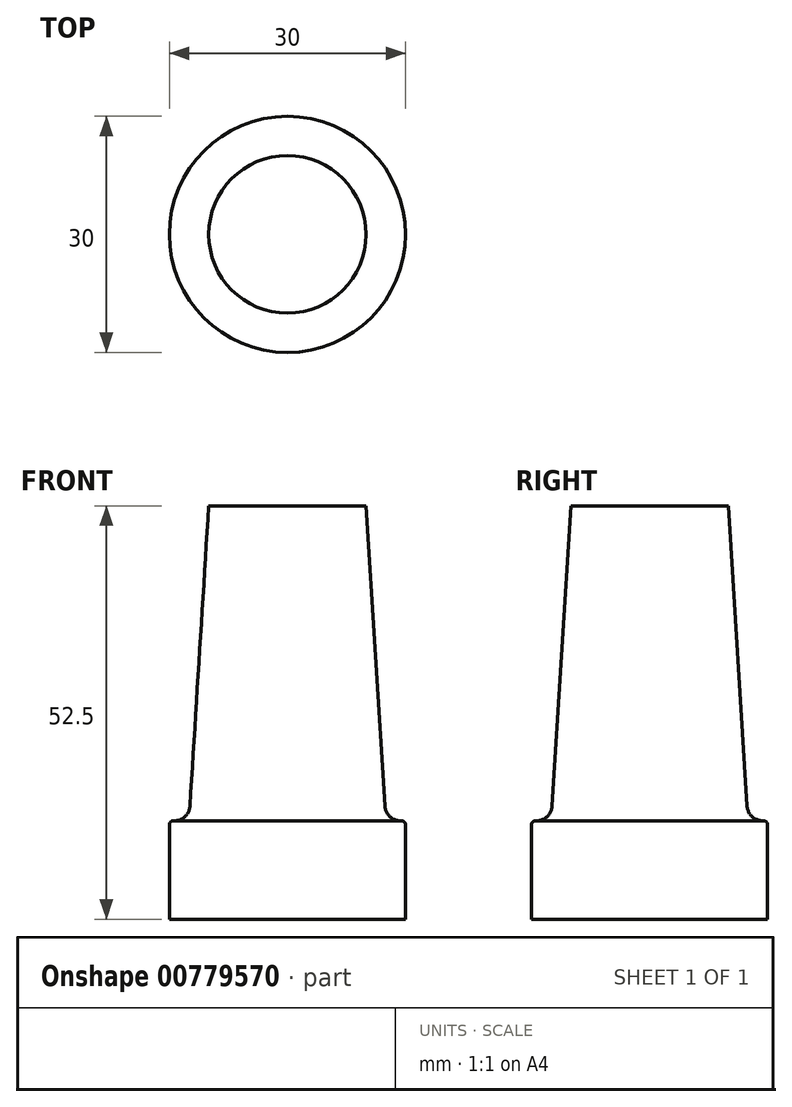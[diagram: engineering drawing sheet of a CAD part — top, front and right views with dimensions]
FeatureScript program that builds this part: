
annotation { "Feature Type Name" : "Feature", "Feature Type Description" : "" }
export const myFeature = defineFeature(function(context is Context, id is Id, definition is map)
    precondition{}
    {
        {
            var Q0;
            Q0=qCreatedBy(makeId("Front.planeOp"),FACE);
            var sketch = newSketch(context, id + "F0", { "sketchPlane" : qUnion([Q0])});
            skLineSegment(sketch, "E0.bottom", {"start": v(0, -7.5) * mm, "end": v(-15, -7.5) * mm});
            skLineSegment(sketch, "E0.left", {"start": v(15, -7.5) * mm, "end": v(15, 7.5) * mm});
            skLineSegment(sketch, "E0.right", {"start": v(-15, -7.5) * mm, "end": v(-15, 4.5) * mm});
            skPoint(sketch, "E0.middle", {"position": v(0, 0) * mm});
            skLineSegment(sketch, "E1", {"start": v(-12.38, 6.88) * mm, "end": v(-10, 45) * mm});
            skLineSegment(sketch, "E2", {"start": v(12.5, 5) * mm, "end": v(10, 45) * mm});
            skLineSegment(sketch, "E3", {"start": v(-10, 45) * mm, "end": v(0, 45) * mm});
            skLineSegment(sketch, "E4", {"start": v(12.5, 5) * mm, "end": v(-12.5, 5) * mm});
            skLineSegment(sketch, "E5", {"start": v(0, 5) * mm, "end": v(0, -7.5) * mm, "construction": true});
            skLineSegment(sketch, "E6", {"start": v(0, 5) * mm, "end": v(0, 45) * mm, "construction": true});
            skArc(sketch, "E7", {"start": v(0, 60) * mm, "mid": v(-7.5, 52.5) * mm, "end": v(0, 45) * mm});
            skLineSegment(sketch, "E8", {"start": v(-14.38, 5) * mm, "end": v(-14.5, 5) * mm});
            skPoint(sketch, "E9.visualSharp", {"position": v(-12.5, 5) * mm});
            skArc(sketch, "E9.filletArc", {"start": v(-14.38, 5) * mm, "mid": v(-13, 5.54) * mm, "end": v(-12.38, 6.88) * mm});
            skArc(sketch, "E10.filletArc", {"start": v(-14.5, 5) * mm, "mid": v(-14.85, 4.85) * mm, "end": v(-15, 4.5) * mm});
            skLineSegment(sketch, "E11", {"start": v(-12.5, 5) * mm, "end": v(-14.38, 5) * mm});
            skLineSegment(sketch, "E12", {"start": v(0, 60) * mm, "end": v(0, -12.12) * mm});
            skSolve(sketch);
        }
        {
            var Q0;
            Q0=sQuery(id+"F0.wireOp",EDGE,"E3");
            var Q1;
            Q1=sQuery(id+"F0.wireOp",EDGE,"E1");
            var Q2;
            Q2=sQuery(id+"F0.wireOp",EDGE,"E9.filletArc");
            var Q3;
            Q3=sQuery(id+"F0.wireOp",EDGE,"E8");
            var Q4;
            Q4=sQuery(id+"F0.wireOp",EDGE,"E10.filletArc");
            var Q5;
            Q5=sQuery(id+"F0.wireOp",EDGE,"E0.right");
            var Q6;
            Q6=sQuery(id+"F0.wireOp",EDGE,"E0.bottom");
            var Q7;
            Q7=sQuery(id+"F0.wireOp",EDGE,"E12");
            revolve(context, id + "F1", {"bodyType" : ToolBodyType.SURFACE, "surfaceOperationType" : NewSurfaceOperationType.NEW, "surfaceEntities" : qUnion([Q0, Q1, Q2, Q3, Q4, Q5, Q6]), "axis" : qUnion([Q7]), "revolveType" : RevolveType.FULL});
        }
    });
